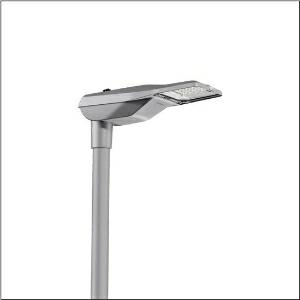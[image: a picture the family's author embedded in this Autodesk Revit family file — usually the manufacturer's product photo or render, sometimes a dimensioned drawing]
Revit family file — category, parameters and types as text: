
# Revit family: streetlight_sl_21_micro___p0_8a_5xe1u33s08db_860c
name_source: partatom
category: Lighting Fixtures
units: mm (PartAtom-declared; Revit-internal decimal feet)

## family parameters
Cut with Voids When Loaded = No
Host = Face
Light Source = No
Part Type = Normal
Room Calculation Point = No
Round Connector Dimension = Use Diameter
Shared = No

## types (1)
- --- (1 x LED, 5040 lm, 39.1 W, 3000K)
    Apparent Load = 39 VA
    CIE Flux Codes = 33 69 96 100 100
    Color Rendering = 70
    Color Temperature = 3000K
    Default Elevation = 1800 mm
    Description = Streetlight SL 21 micro, mast luminaire, primary light control with lens, of PMMA, primary optical cover: cover, of toughened safety glass, transparent, light distribution: P0.8a, light emission: direct distribution, primary light characteristic: asymmetric, installation type: post-top, side-entry, LED, High Power LED, rated luminous flux: 5.040lm, luminous efficacy: 129lm/W, light colour: 730, colour temperature: 3000K, control gear: D4i, control: pre-setting: logarithmic dimming characteristic, flexible luminous flux parameterisation, time-dependent luminous flux control, constant luminous flux control, overheat protection, mains connection: 220..240V, AC, 50/60Hz, start of lifetime: 39W, end of service life: 41W, reduction: 18W, luminaire housing, of diecast aluminium, powder-coated, Siteco® metallic grey (DB 702S), corrosivity category C5 mid according to DIN EN ISO 12944, multi-level sealing system, sealing non-destructively replaceable, inclination adjustable: 0°, 5°, 10°, 15°, please order mast flange separately, length: 528mm, width: 235mm, height: 110mm, mast flange for spigot size: 42mm (side-entry): 5XC10008XM4, 60/48mm (side-entry/post-top): 5XC10108XM2, 76/60mm (side-entry/post-top): 5XC10108XM1, Smart Interface above, protection rating (complete): IP66, insulation class (complete): insulation class II (safety insulation), certification: CE, ENEC, ENEC+, VDE, impact resistance: IK10, permissible operating ambient temperature for outdoor applications: -40..+50°C, standard-compliant lighting for roads and squares, packaging unit: 1 piece

Light Distribution: P0.8a
    Height = 110 mm
    Lamp = 1 x LED
    Lamp Light Flux = 5040 lm
    Lamp Power = 39.1 W
    Lamp count = 1
    Length = 528 mm
    Luminous efficacy = 129 lm/W
    Manufacturer = Siteco
    ModVariant = No
    Model = 5XE1U33S08DB
    Number of Poles = 1
    OnlyDefault = Yes
    Power Factor = 1
    Product Name = Streetlight SL 21 micro | P0.8a
    Product group = mast luminaire | pylon top
    ProductGroupID = 6100
    Protection Class = Protection class II
    Protection Degree = IP 66
    RLX_Detail_Level = 1
    RLX_Emergency_Light_Flux = 0 lm
    RLX_Emergency_Type = 0
    RLX_Emergency_Type_DB = No
    RlxData = <blob elided: 98177 chars, md5=f2a2a7fc>
    Socket = socket
    Standby Power = 0 W
    System Light Flux = 5040 lm
    System Power = 39 W
    Type Comments = factory setting: luminous flux: 100 % | dim-lin: 254 | 765 mA
    Type Image = l_1277292.jpg
    URL = http://relux.com
    VarID = @adj_072814
    Voltage = 0 V
    Weight = 0.00 kg
    Width = 235 mm

## geometry (parser evidence)
native form markers: Blend x4, Sweep x11
no freeform markers — native parametric forms only
